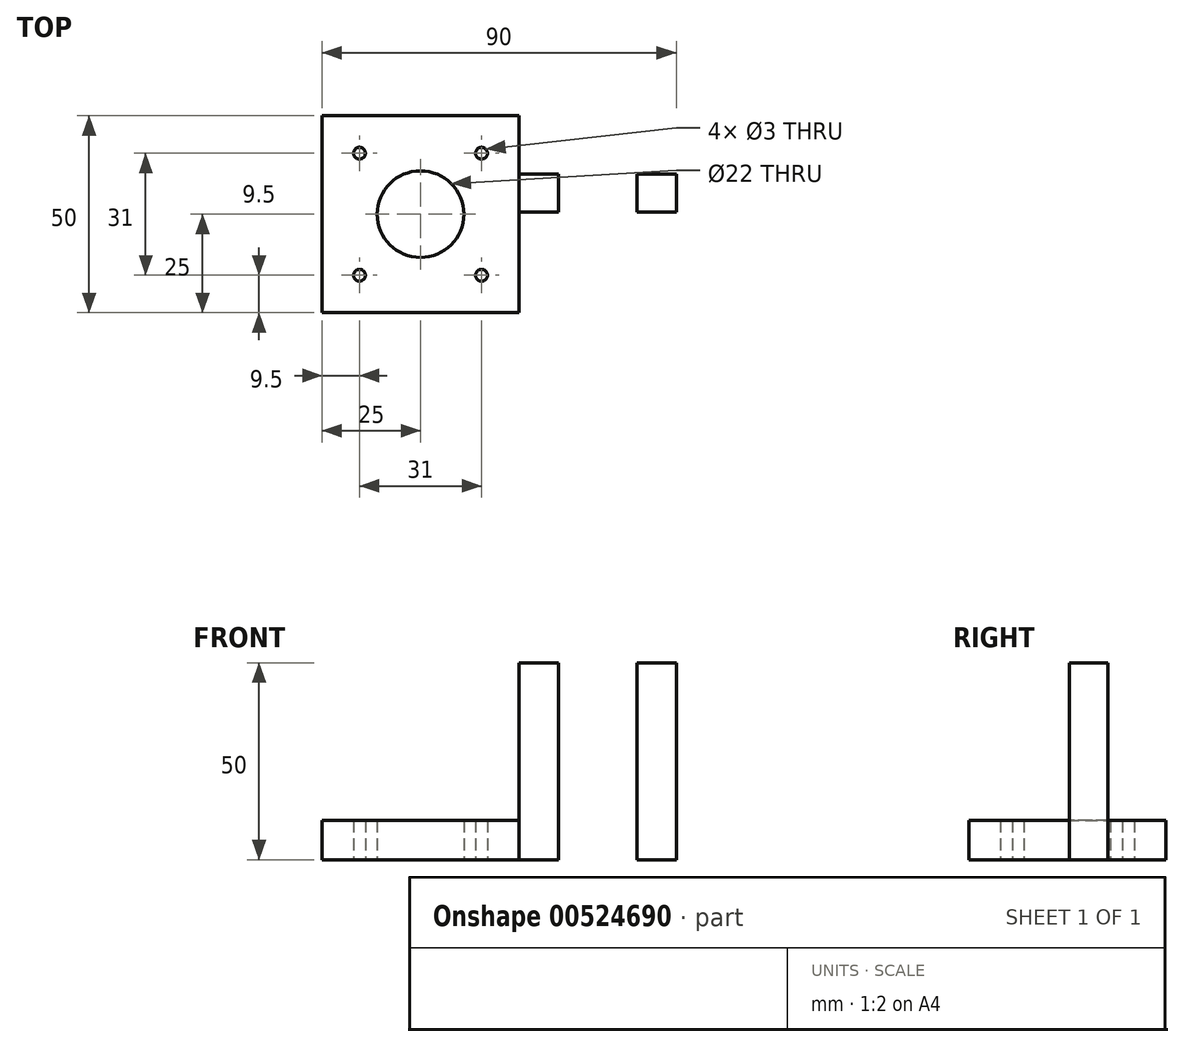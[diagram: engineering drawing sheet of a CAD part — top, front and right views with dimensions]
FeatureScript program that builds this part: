
annotation { "Feature Type Name" : "Feature", "Feature Type Description" : "" }
export const myFeature = defineFeature(function(context is Context, id is Id, definition is map)
    precondition{}
    {
        {
            var Q0;
            Q0=qCreatedBy(makeId("Top.planeOp"),FACE);
            var sketch = newSketch(context, id + "F0", { "sketchPlane" : qUnion([Q0])});
            skLineSegment(sketch, "E0.bottom", {"start": v(-31.94, 45) * mm, "end": v(18.06, 45) * mm});
            skLineSegment(sketch, "E0.top", {"start": v(-31.94, -5) * mm, "end": v(18.06, -5) * mm});
            skLineSegment(sketch, "E0.left", {"start": v(-31.94, 45) * mm, "end": v(-31.94, -5) * mm});
            skLineSegment(sketch, "E0.right", {"start": v(18.06, 45) * mm, "end": v(18.06, -5) * mm});
            skLineSegment(sketch, "E1.bottom", {"start": v(18.06, 40) * mm, "end": v(58.06, 40) * mm});
            skLineSegment(sketch, "E1.left", {"start": v(18.06, 40) * mm, "end": v(18.06, 0) * mm});
            skLineSegment(sketch, "E1.right", {"start": v(58.06, 40) * mm, "end": v(58.06, 0) * mm});
            skLineSegment(sketch, "E2.bottom", {"start": v(18.06, 20.5) * mm, "end": v(28.06, 20.5) * mm});
            skLineSegment(sketch, "E2.top", {"start": v(18.06, 40) * mm, "end": v(28.06, 40) * mm});
            skLineSegment(sketch, "E2.left", {"start": v(18.06, 20.5) * mm, "end": v(18.06, 40) * mm});
            skLineSegment(sketch, "E2.right", {"start": v(28.06, 20.5) * mm, "end": v(28.06, 40) * mm});
            skLineSegment(sketch, "E3.bottom", {"start": v(18.06, 30.25) * mm, "end": v(58.06, 30.25) * mm});
            skLineSegment(sketch, "E3.left", {"start": v(18.06, 30.25) * mm, "end": v(18.06, 40) * mm});
            skLineSegment(sketch, "E3.right", {"start": v(58.06, 30.25) * mm, "end": v(58.06, 40) * mm});
            skPoint(sketch, "E4", {"position": v(28.06, 30.25) * mm});
            skLineSegment(sketch, "E5.bottom", {"start": v(58.06, 40) * mm, "end": v(48.06, 40) * mm});
            skLineSegment(sketch, "E5.top", {"start": v(58.06, 20.5) * mm, "end": v(48.06, 20.5) * mm});
            skLineSegment(sketch, "E5.left", {"start": v(58.06, 40) * mm, "end": v(58.06, 20.5) * mm});
            skLineSegment(sketch, "E5.right", {"start": v(48.06, 40) * mm, "end": v(48.06, 20.5) * mm});
            skCircle(sketch, "E6", {"center": v(-6.94, 20) * mm, "radius": 11 * mm});
            skSolve(sketch);
        }
        {
            var Q0;
            {var subQ1=sQuery(id+"F0.wireOp",EDGE,"E0.bottom");Q0=makeQuery(id+"F0.imprint","IMPRINT",FACE,{"disambiguationData":[TD([[makeQuery(id+"F0.imprint","IMPRINT",EDGE,{"derivedFrom":subQ1}),-1.0]])]});}
            extrude(context, id + "F1", {"entities" : qUnion([Q0]), "depth" : 10 * mm, "offsetDistance" : 25 * mm});
        }
        {
            var Q0;
            Q0=makeQuery(id+"F1.opExtrude","CAP_FACE",FACE,{"disambiguationData":[OSD([sQuery(id+"F0.wireOp",EDGE,"E0.bottom"),sQuery(id+"F0.wireOp",EDGE,"E0.top"),sQuery(id+"F0.wireOp",EDGE,"E0.left"),sQuery(id+"F0.wireOp",EDGE,"E0.right")])],"isStart":true});
            var sketch = newSketch(context, id + "F2", { "sketchPlane" : qUnion([Q0])});
            skPoint(sketch, "E7", {"position": v(-22.44, -35.5) * mm});
            skPoint(sketch, "E8", {"position": v(8.56, -35.5) * mm});
            skPoint(sketch, "E9", {"position": v(-22.44, -4.5) * mm});
            skPoint(sketch, "E10", {"position": v(8.56, -4.5) * mm});
            skPoint(sketch, "E11", {"position": v(-6.94, -20) * mm});
            skSolve(sketch);
        }
        {
            var Q0;
            Q0=sQuery(id+"F2.wireOp",VERTEX,"E10");
            var Q1;
            Q1=sQuery(id+"F2.wireOp",VERTEX,"E9");
            var Q2;
            Q2=sQuery(id+"F2.wireOp",VERTEX,"E7");
            var Q3;
            Q3=sQuery(id+"F2.wireOp",VERTEX,"E8");
            var Q4;
            Q4=makeQuery(id+"F1.opExtrude","SWEPT_BODY",BODY,{"disambiguationData":[OSD([sQuery(id+"F0.wireOp",EDGE,"E0.bottom"),sQuery(id+"F0.wireOp",EDGE,"E0.top"),sQuery(id+"F0.wireOp",EDGE,"E0.left"),sQuery(id+"F0.wireOp",EDGE,"E0.right")])]});
            hole(context, id + "F3", {"style" : HoleStyle.SIMPLE, "endStyle" : HoleEndStyle.THROUGH, "holeDiameter" : 3 * mm, "isTappedThrough" : true, "tappedDepth" : 12 * mm, "tapClearance" : 3, "startFromSketch" : true, "locations" : qUnion([Q0, Q1, Q2, Q3]), "scope" : qUnion([Q4])});
        }
        {
            var Q0;
            {var subQ0=sQuery(id+"F0.wireOp",EDGE,"E2.bottom");Q0=makeQuery(id+"F0.imprint","IMPRINT",FACE,{"disambiguationData":[TD([[makeQuery(id+"F0.imprint","IMPRINT",EDGE,{"derivedFrom":subQ0}),1.0]])]});}
            var Q1;
            {var subQ5=sQuery(id+"F0.wireOp",EDGE,"E3.left");Q1=makeQuery(id+"F0.imprint","IMPRINT",FACE,{"disambiguationData":[TD([[makeQuery(id+"F0.imprint","IMPRINT",EDGE,{"derivedFrom":subQ5}),-1.0]])]});}
            var Q2;
            {var subQ0=sQuery(id+"F0.wireOp",EDGE,"E1.bottom");var subQ1=sQuery(id+"F0.wireOp",EDGE,"E2.right");var subQ2=makeQuery(id+"F0.imprint","INTERSECT",VERTEX,{"derivedFrom":[subQ1,subQ0]});Q2=makeQuery(id+"F0.imprint","IMPRINT",FACE,{"disambiguationData":[TD([[makeQuery(id+"F0.imprint","IMPRINT",EDGE,{"disambiguationData":[TD([[subQ2,1.0]])],"derivedFrom":subQ1}),-1.0]])]});}
            var Q3;
            {var subQ5=sQuery(id+"F0.wireOp",EDGE,"E5.bottom");Q3=makeQuery(id+"F0.imprint","IMPRINT",FACE,{"disambiguationData":[TD([[makeQuery(id+"F0.imprint","IMPRINT",EDGE,{"derivedFrom":subQ5}),1.0]])]});}
            var Q4;
            {var subQ5=sQuery(id+"F0.wireOp",EDGE,"E5.top");Q4=makeQuery(id+"F0.imprint","IMPRINT",FACE,{"disambiguationData":[TD([[makeQuery(id+"F0.imprint","IMPRINT",EDGE,{"derivedFrom":subQ5}),-1.0]])]});}
            extrude(context, id + "F4", {"entities" : qUnion([Q0, Q1, Q2, Q3, Q4]), "operationType" : NewBodyOperationType.ADD, "depth" : 50 * mm, "offsetDistance" : 25 * mm});
        }
        {
            var Q0;
            Q0=makeQuery(id+"F4.opExtrude","SWEPT_FACE",FACE,{"disambiguationData":[OSD([sQuery(id+"F0.wireOp",EDGE,"E1.bottom"),sQuery(id+"F0.wireOp",EDGE,"E5.bottom")])]});
            var sketch = newSketch(context, id + "F5", { "sketchPlane" : qUnion([Q0])});
            skLineSegment(sketch, "E12", {"start": v(-23.06, 40) * mm, "end": v(-26.06, 38.27) * mm});
            skLineSegment(sketch, "E13", {"start": v(-26.06, 38.27) * mm, "end": v(-26.06, 34.8) * mm});
            skLineSegment(sketch, "E14", {"start": v(-26.06, 34.8) * mm, "end": v(-23.06, 33.07) * mm});
            skLineSegment(sketch, "E15", {"start": v(-23.06, 33.07) * mm, "end": v(-20.06, 34.8) * mm});
            skLineSegment(sketch, "E16", {"start": v(-20.06, 34.8) * mm, "end": v(-20.06, 38.27) * mm});
            skLineSegment(sketch, "E17", {"start": v(-20.06, 38.27) * mm, "end": v(-23.06, 40) * mm});
            skCircle(sketch, "E18", {"center": v(-23.06, 36.54) * mm, "radius": 1.5 * mm});
            skLineSegment(sketch, "E19", {"start": v(-23.06, 26.93) * mm, "end": v(-26.06, 25.2) * mm});
            skLineSegment(sketch, "E20", {"start": v(-26.06, 25.2) * mm, "end": v(-26.06, 21.73) * mm});
            skLineSegment(sketch, "E21", {"start": v(-26.06, 21.73) * mm, "end": v(-23.06, 20) * mm});
            skLineSegment(sketch, "E22", {"start": v(-23.06, 20) * mm, "end": v(-20.06, 21.73) * mm});
            skLineSegment(sketch, "E23", {"start": v(-20.06, 21.73) * mm, "end": v(-20.06, 25.2) * mm});
            skLineSegment(sketch, "E24", {"start": v(-20.06, 25.2) * mm, "end": v(-23.06, 26.93) * mm});
            skCircle(sketch, "E25", {"center": v(-23.06, 23.46) * mm, "radius": 1.5 * mm});
            skLineSegment(sketch, "E26", {"start": v(-53.06, 20) * mm, "end": v(-50.06, 21.73) * mm});
            skLineSegment(sketch, "E27", {"start": v(-50.06, 21.73) * mm, "end": v(-50.06, 25.2) * mm});
            skLineSegment(sketch, "E28", {"start": v(-50.06, 25.2) * mm, "end": v(-53.06, 26.93) * mm});
            skLineSegment(sketch, "E29", {"start": v(-53.06, 26.93) * mm, "end": v(-56.06, 25.2) * mm});
            skLineSegment(sketch, "E30", {"start": v(-56.06, 25.2) * mm, "end": v(-56.06, 21.73) * mm});
            skLineSegment(sketch, "E31", {"start": v(-56.06, 21.73) * mm, "end": v(-53.06, 20) * mm});
            skCircle(sketch, "E32", {"center": v(-53.06, 23.46) * mm, "radius": 1.5 * mm});
            skLineSegment(sketch, "E33", {"start": v(-53.06, 33.07) * mm, "end": v(-50.06, 34.8) * mm});
            skLineSegment(sketch, "E34", {"start": v(-50.06, 34.8) * mm, "end": v(-50.06, 38.27) * mm});
            skLineSegment(sketch, "E35", {"start": v(-50.06, 38.27) * mm, "end": v(-53.06, 40) * mm});
            skLineSegment(sketch, "E36", {"start": v(-53.06, 40) * mm, "end": v(-56.06, 38.27) * mm});
            skLineSegment(sketch, "E37", {"start": v(-56.06, 38.27) * mm, "end": v(-56.06, 34.8) * mm});
            skLineSegment(sketch, "E38", {"start": v(-56.06, 34.8) * mm, "end": v(-53.06, 33.07) * mm});
            skCircle(sketch, "E39", {"center": v(-53.06, 36.54) * mm, "radius": 1.5 * mm});
            skSolve(sketch);
        }
        {
            var Q0;
            Q0=makeQuery(id+"F5.imprint","IMPRINT",FACE,{"disambiguationData":[TD([[makeQuery(id+"F5.imprint","IMPRINT",EDGE,{"derivedFrom":sQuery(id+"F5.wireOp",EDGE,"E19")}),1.0]])]});
            var Q1;
            Q1=makeQuery(id+"F5.imprint","IMPRINT",FACE,{"disambiguationData":[TD([[makeQuery(id+"F5.imprint","IMPRINT",EDGE,{"derivedFrom":sQuery(id+"F5.wireOp",EDGE,"E12")}),1.0]])]});
            var Q2;
            Q2=makeQuery(id+"F5.imprint","IMPRINT",FACE,{"disambiguationData":[TD([[makeQuery(id+"F5.imprint","IMPRINT",EDGE,{"derivedFrom":sQuery(id+"F5.wireOp",EDGE,"E33")}),1.0]])]});
            var Q3;
            Q3=makeQuery(id+"F5.imprint","IMPRINT",FACE,{"disambiguationData":[TD([[makeQuery(id+"F5.imprint","IMPRINT",EDGE,{"derivedFrom":sQuery(id+"F5.wireOp",EDGE,"E26")}),1.0]])]});
            extrude(context, id + "F6", {"entities" : qUnion([Q0, Q1, Q2, Q3]), "operationType" : NewBodyOperationType.REMOVE, "oppositeDirection" : true, "depth" : 3 * mm, "offsetDistance" : 25 * mm});
        }
        {
            var Q0;
            Q0=makeQuery(id+"F6.boolean.opBoolean","SPLIT",FACE,{"disambiguationData":[TD([makeQuery(id+"F6.opExtrude","SWEPT_FACE",FACE,{"disambiguationData":[OSD([sQuery(id+"F5.wireOp",EDGE,"E25")])]})])],"derivedFrom":makeQuery(id+"F4.opExtrude","SWEPT_FACE",FACE,{"disambiguationData":[OSD([sQuery(id+"F0.wireOp",EDGE,"E1.bottom"),sQuery(id+"F0.wireOp",EDGE,"E5.bottom")])]})});
            var Q1;
            Q1=makeQuery(id+"F6.boolean.opBoolean","SPLIT",FACE,{"disambiguationData":[TD([makeQuery(id+"F6.opExtrude","SWEPT_FACE",FACE,{"disambiguationData":[OSD([sQuery(id+"F5.wireOp",EDGE,"E18")])]})])],"derivedFrom":makeQuery(id+"F4.opExtrude","SWEPT_FACE",FACE,{"disambiguationData":[OSD([sQuery(id+"F0.wireOp",EDGE,"E1.bottom"),sQuery(id+"F0.wireOp",EDGE,"E5.bottom")])]})});
            var Q2;
            Q2=makeQuery(id+"F6.boolean.opBoolean","SPLIT",FACE,{"disambiguationData":[TD([makeQuery(id+"F6.opExtrude","SWEPT_FACE",FACE,{"disambiguationData":[OSD([sQuery(id+"F5.wireOp",EDGE,"E39")])]})])],"derivedFrom":makeQuery(id+"F4.opExtrude","SWEPT_FACE",FACE,{"disambiguationData":[OSD([sQuery(id+"F0.wireOp",EDGE,"E1.bottom"),sQuery(id+"F0.wireOp",EDGE,"E5.bottom")])]})});
            var Q3;
            Q3=makeQuery(id+"F6.boolean.opBoolean","SPLIT",FACE,{"disambiguationData":[TD([makeQuery(id+"F6.opExtrude","SWEPT_FACE",FACE,{"disambiguationData":[OSD([sQuery(id+"F5.wireOp",EDGE,"E32")])]})])],"derivedFrom":makeQuery(id+"F4.opExtrude","SWEPT_FACE",FACE,{"disambiguationData":[OSD([sQuery(id+"F0.wireOp",EDGE,"E1.bottom"),sQuery(id+"F0.wireOp",EDGE,"E5.bottom")])]})});
            extrude(context, id + "F7", {"entities" : qUnion([Q0, Q1, Q2, Q3]), "operationType" : NewBodyOperationType.REMOVE, "oppositeDirection" : true, "depth" : 20 * mm, "offsetDistance" : 25 * mm});
        }
    });
